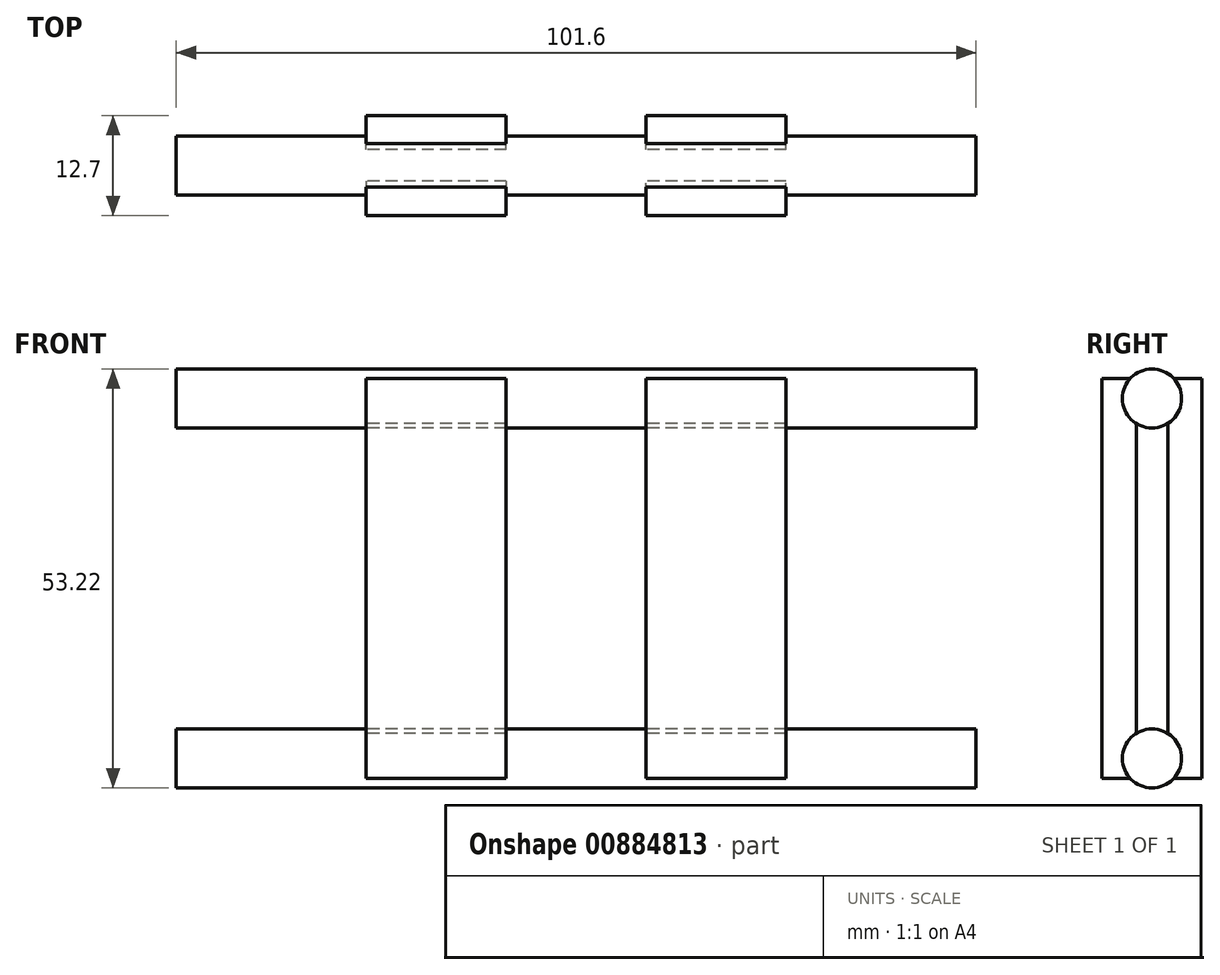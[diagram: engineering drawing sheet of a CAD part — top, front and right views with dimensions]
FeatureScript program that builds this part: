
annotation { "Feature Type Name" : "Feature", "Feature Type Description" : "" }
export const myFeature = defineFeature(function(context is Context, id is Id, definition is map)
    precondition{}
    {
        {
            var Q0;
            Q0=qCreatedBy(makeId("Top.planeOp"),FACE);
            var sketch = newSketch(context, id + "F0", { "sketchPlane" : qUnion([Q0])});
            skLineSegment(sketch, "E0.bottom", {"start": v(50.8, -2) * mm, "end": v(-50.8, -2) * mm});
            skLineSegment(sketch, "E0.top", {"start": v(50.8, 2) * mm, "end": v(-50.8, 2) * mm});
            skLineSegment(sketch, "E0.left", {"start": v(50.8, -2) * mm, "end": v(50.8, 2) * mm});
            skLineSegment(sketch, "E0.right", {"start": v(-50.8, -2) * mm, "end": v(-50.8, 2) * mm});
            skPoint(sketch, "E0.middle", {"position": v(0, 0) * mm});
            skLineSegment(sketch, "E1.bottom", {"start": v(-8.89, -6.35) * mm, "end": v(-26.67, -6.35) * mm});
            skLineSegment(sketch, "E1.top", {"start": v(-8.9, 6.35) * mm, "end": v(-26.67, 6.35) * mm});
            skLineSegment(sketch, "E1.left", {"start": v(-8.9, -6.35) * mm, "end": v(-8.9, 6.35) * mm});
            skLineSegment(sketch, "E1.right", {"start": v(-26.67, -6.35) * mm, "end": v(-26.67, 6.35) * mm});
            skPoint(sketch, "E1.middle", {"position": v(-17.78, 0) * mm});
            skLineSegment(sketch, "E2.bottom", {"start": v(26.67, -6.35) * mm, "end": v(8.89, -6.35) * mm});
            skLineSegment(sketch, "E2.top", {"start": v(26.67, 6.35) * mm, "end": v(8.89, 6.35) * mm});
            skLineSegment(sketch, "E2.left", {"start": v(26.67, -6.35) * mm, "end": v(26.67, 6.35) * mm});
            skLineSegment(sketch, "E2.right", {"start": v(8.89, -6.35) * mm, "end": v(8.89, 6.35) * mm});
            skPoint(sketch, "E2.middle", {"position": v(17.78, 0) * mm});
            skSolve(sketch);
        }
        {
            var Q0;
            Q0=makeQuery(id+"F0.imprint","IMPRINT",FACE,{"disambiguationData":[TD([[makeQuery(id+"F0.imprint","IMPRINT",EDGE,{"derivedFrom":sQuery(id+"F0.wireOp",EDGE,"E0.bottom")}),-1.0]])]});
            extrude(context, id + "F1", {"entities" : qUnion([Q0]), "depth" : 5.08 * mm, "offsetDistance" : 25.4 * mm});
        }
        {
            var Q0;
            Q0=makeQuery(id+"F0.imprint","IMPRINT",FACE,{"disambiguationData":[TD([[makeQuery(id+"F0.imprint","IMPRINT",EDGE,{"derivedFrom":sQuery(id+"F0.wireOp",EDGE,"E1.bottom")}),-1.0]])]});
            var Q1;
            Q1=makeQuery(id+"F0.imprint","IMPRINT",FACE,{"disambiguationData":[TD([[makeQuery(id+"F0.imprint","IMPRINT",EDGE,{"derivedFrom":sQuery(id+"F0.wireOp",EDGE,"E2.bottom")}),-1.0]])]});
            var Q2;
            {var subQ5=sQuery(id+"F0.wireOp",EDGE,"E1.top");Q2=makeQuery(id+"F0.imprint","IMPRINT",FACE,{"disambiguationData":[TD([[makeQuery(id+"F0.imprint","IMPRINT",EDGE,{"derivedFrom":subQ5}),1.0]])]});}
            var Q3;
            {var subQ5=sQuery(id+"F0.wireOp",EDGE,"E2.top");Q3=makeQuery(id+"F0.imprint","IMPRINT",FACE,{"disambiguationData":[TD([[makeQuery(id+"F0.imprint","IMPRINT",EDGE,{"derivedFrom":subQ5}),1.0]])]});}
            extrude(context, id + "F2", {"entities" : qUnion([Q0, Q1, Q2, Q3]), "operationType" : NewBodyOperationType.ADD, "depth" : 50.8 * mm, "offsetDistance" : 25.4 * mm});
        }
        {
            var Q0;
            Q0=makeQuery(id+"F1.opExtrude","SWEPT_FACE",FACE,{"disambiguationData":[OSD([sQuery(id+"F0.wireOp",EDGE,"E0.right")])]});
            var sketch = newSketch(context, id + "F3", { "sketchPlane" : qUnion([Q0])});
            skCircle(sketch, "E3", {"center": v(0, 2.54) * mm, "radius": 3.75 * mm});
            skSolve(sketch);
        }
        {
            var Q0;
            {var subQ0=sQuery(id+"F3.wireOp",EDGE,"E3");var subQ1=makeQuery(id+"F1.opExtrude","CAP_EDGE",EDGE,{"disambiguationData":[OSD([sQuery(id+"F0.wireOp",EDGE,"E0.right")])],"isStart":true});var subQ2=makeQuery(id+"F3.imprint","INTERSECT",VERTEX,{"disambiguationData":[OD(0.0)],"derivedFrom":[subQ1,subQ0]});Q0=makeQuery(id+"F3.imprint","IMPRINT",FACE,{"disambiguationData":[TD([[makeQuery(id+"F3.imprint","IMPRINT",EDGE,{"disambiguationData":[TD([[subQ2,-1.0]])],"derivedFrom":subQ0}),1.0]])]});}
            var Q1;
            {var subQ0=sQuery(id+"F3.wireOp",EDGE,"E3");var subQ1=sQuery(id+"F0.wireOp",EDGE,"E0.right");var subQ3=makeQuery(id+"F1.opExtrude","CAP_EDGE",EDGE,{"disambiguationData":[OSD([subQ1])],"isStart":true});var subQ4=makeQuery(id+"F3.imprint","INTERSECT",VERTEX,{"disambiguationData":[OD(0.0)],"derivedFrom":[subQ3,subQ0]});Q1=makeQuery(id+"F3.imprint","IMPRINT",FACE,{"disambiguationData":[TD([[makeQuery(id+"F3.imprint","IMPRINT",EDGE,{"disambiguationData":[TD([[subQ4,1.0]])],"derivedFrom":subQ3}),-1.0]])]});}
            var Q2;
            {var subQ0=sQuery(id+"F3.wireOp",EDGE,"E3");var subQ1=makeQuery(id+"F1.opExtrude","CAP_EDGE",EDGE,{"disambiguationData":[OSD([sQuery(id+"F0.wireOp",EDGE,"E0.right")])],"isStart":false});var subQ2=makeQuery(id+"F3.imprint","INTERSECT",VERTEX,{"disambiguationData":[OD(0.0)],"derivedFrom":[subQ1,subQ0]});Q2=makeQuery(id+"F3.imprint","IMPRINT",FACE,{"disambiguationData":[TD([[makeQuery(id+"F3.imprint","IMPRINT",EDGE,{"disambiguationData":[TD([[subQ2,-1.0]])],"derivedFrom":subQ0}),1.0]])]});}
            extrude(context, id + "F4", {"entities" : qUnion([Q0, Q1, Q2]), "operationType" : NewBodyOperationType.ADD, "oppositeDirection" : true, "depth" : 101.6 * mm, "offsetDistance" : 25.4 * mm});
        }
        {
            var Q0;
            Q0=makeQuery(id+"F2.opExtrude","CAP_FACE",FACE,{"disambiguationData":[OSD([sQuery(id+"F0.wireOp",EDGE,"E1.bottom"),sQuery(id+"F0.wireOp",EDGE,"E1.top"),sQuery(id+"F0.wireOp",EDGE,"E1.left"),sQuery(id+"F0.wireOp",EDGE,"E1.right")])],"isStart":false});
            var sketch = newSketch(context, id + "F5", { "sketchPlane" : qUnion([Q0])});
            skLineSegment(sketch, "E4.bottom", {"start": v(50.8, -2) * mm, "end": v(-50.8, -2) * mm});
            skLineSegment(sketch, "E4.top", {"start": v(50.8, 2) * mm, "end": v(-50.8, 2) * mm});
            skLineSegment(sketch, "E4.left", {"start": v(50.8, -2) * mm, "end": v(50.8, 2) * mm});
            skLineSegment(sketch, "E4.right", {"start": v(-50.8, -2) * mm, "end": v(-50.8, 2) * mm});
            skPoint(sketch, "E4.middle", {"position": v(0, 0) * mm});
            skSolve(sketch);
        }
        {
            var Q0;
            Q0=makeQuery(id+"F5.imprint","IMPRINT",FACE,{"disambiguationData":[TD([[makeQuery(id+"F5.imprint","IMPRINT",EDGE,{"derivedFrom":sQuery(id+"F5.wireOp",EDGE,"E4.bottom")}),-1.0]])]});
            extrude(context, id + "F6", {"entities" : qUnion([Q0]), "operationType" : NewBodyOperationType.ADD, "oppositeDirection" : true, "depth" : 5.08 * mm, "offsetDistance" : 25.4 * mm});
        }
        {
            var Q0;
            Q0=makeQuery(id+"F6.opExtrude","SWEPT_FACE",FACE,{"disambiguationData":[OSD([sQuery(id+"F5.wireOp",EDGE,"E4.right")])]});
            var sketch = newSketch(context, id + "F7", { "sketchPlane" : qUnion([Q0])});
            skCircle(sketch, "E5", {"center": v(0, 48.26) * mm, "radius": 3.75 * mm});
            skSolve(sketch);
        }
        {
            var Q0;
            Q0=makeQuery(id+"F7.imprint","IMPRINT",FACE,{"disambiguationData":[TD([[makeQuery(id+"F7.imprint","IMPRINT",EDGE,{"derivedFrom":sQuery(id+"F7.wireOp",EDGE,"E5")}),1.0]])]});
            extrude(context, id + "F8", {"entities" : qUnion([Q0]), "operationType" : NewBodyOperationType.ADD, "oppositeDirection" : true, "depth" : 101.6 * mm, "offsetDistance" : 25.4 * mm});
        }
    });
